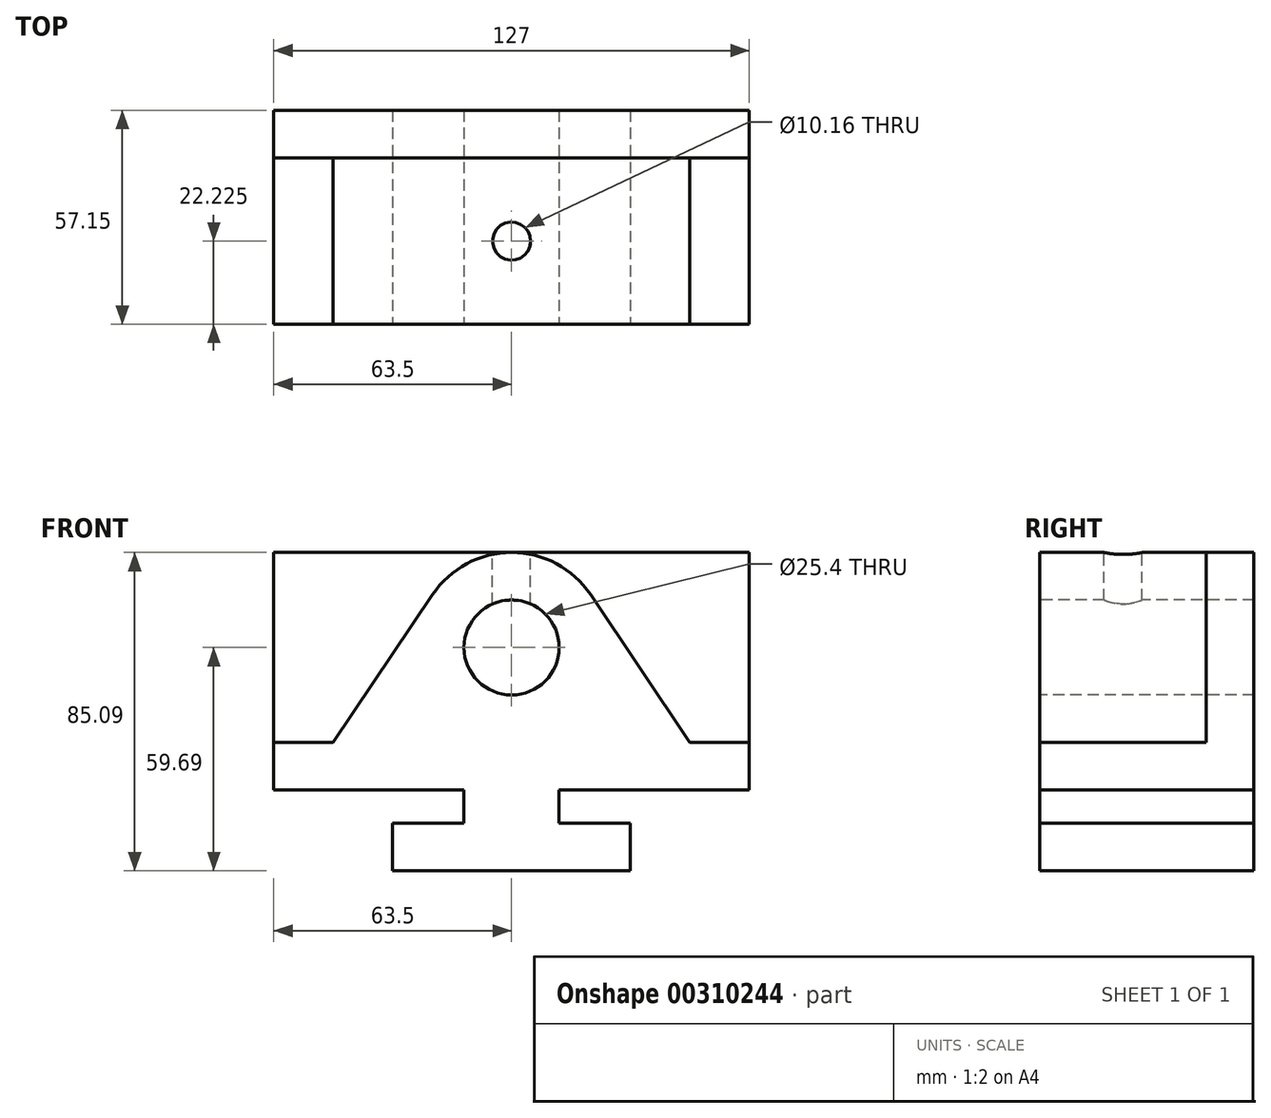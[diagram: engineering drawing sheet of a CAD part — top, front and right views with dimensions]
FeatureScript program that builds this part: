
annotation { "Feature Type Name" : "Feature", "Feature Type Description" : "" }
export const myFeature = defineFeature(function(context is Context, id is Id, definition is map)
    precondition{}
    {
        {
            var Q0;
            Q0=qCreatedBy(makeId("Front.planeOp"),FACE);
            var sketch = newSketch(context, id + "F0", { "sketchPlane" : qUnion([Q0])});
            skLineSegment(sketch, "E0", {"start": v(31.75, 0) * mm, "end": v(-31.75, 0) * mm});
            skLineSegment(sketch, "E1", {"start": v(-31.75, 0) * mm, "end": v(-31.75, 12.7) * mm});
            skLineSegment(sketch, "E2", {"start": v(-31.75, 12.7) * mm, "end": v(-12.7, 12.7) * mm});
            skLineSegment(sketch, "E3", {"start": v(-12.7, 12.7) * mm, "end": v(-12.7, 21.59) * mm});
            skLineSegment(sketch, "E4", {"start": v(-12.7, 21.59) * mm, "end": v(-63.5, 21.59) * mm});
            skLineSegment(sketch, "E5", {"start": v(-63.5, 21.59) * mm, "end": v(-63.5, 85.1) * mm});
            skLineSegment(sketch, "E6", {"start": v(-63.5, 85.1) * mm, "end": v(63.5, 85.1) * mm});
            skLineSegment(sketch, "E7", {"start": v(63.5, 85.1) * mm, "end": v(63.5, 21.6) * mm});
            skLineSegment(sketch, "E8", {"start": v(63.5, 21.6) * mm, "end": v(12.7, 21.59) * mm});
            skLineSegment(sketch, "E9", {"start": v(12.7, 21.59) * mm, "end": v(12.7, 12.7) * mm});
            skLineSegment(sketch, "E10", {"start": v(12.7, 12.7) * mm, "end": v(31.75, 12.7) * mm});
            skLineSegment(sketch, "E11", {"start": v(31.75, 12.7) * mm, "end": v(31.75, 0) * mm});
            skSolve(sketch);
        }
        {
            var Q0;
            Q0 = qSketchRegion(id + "F0", true);
            extrude(context, id + "F1", {"entities" : qUnion([Q0]), "oppositeDirection" : true, "depth" : 57.15 * mm});
        }
        {
            var Q0;
            Q0=makeQuery(id+"F1.opExtrude","CAP_FACE",FACE,{"disambiguationData":[OSD([sQuery(id+"F0.wireOp",EDGE,"E0"),sQuery(id+"F0.wireOp",EDGE,"E1"),sQuery(id+"F0.wireOp",EDGE,"E2"),sQuery(id+"F0.wireOp",EDGE,"E3"),sQuery(id+"F0.wireOp",EDGE,"E4"),sQuery(id+"F0.wireOp",EDGE,"E5"),sQuery(id+"F0.wireOp",EDGE,"E6"),sQuery(id+"F0.wireOp",EDGE,"E7"),sQuery(id+"F0.wireOp",EDGE,"E8"),sQuery(id+"F0.wireOp",EDGE,"E9"),sQuery(id+"F0.wireOp",EDGE,"E10"),sQuery(id+"F0.wireOp",EDGE,"E11")])],"isStart":true});
            var sketch = newSketch(context, id + "F2", { "sketchPlane" : qUnion([Q0])});
            skLineSegment(sketch, "E12", {"start": v(-63.5, 21.59) * mm, "end": v(-63.5, 34.3) * mm});
            skLineSegment(sketch, "E13", {"start": v(-63.5, 34.3) * mm, "end": v(-47.63, 34.3) * mm});
            skLineSegment(sketch, "E14", {"start": v(-47.63, 34.3) * mm, "end": v(-21.1, 73.84) * mm});
            skLineSegment(sketch, "E15", {"start": v(63.5, 21.6) * mm, "end": v(63.5, 34.3) * mm});
            skPoint(sketch, "E15.endSnap0", {"position": v(-55.56, 34.3) * mm});
            skLineSegment(sketch, "E16", {"start": v(63.5, 34.3) * mm, "end": v(47.62, 34.3) * mm});
            skLineSegment(sketch, "E17", {"start": v(47.63, 34.3) * mm, "end": v(21.1, 73.84) * mm});
            skArc(sketch, "E18", {"start": v(21.1, 73.84) * mm, "mid": v(0, 85.1) * mm, "end": v(-21.1, 73.84) * mm});
            skCircle(sketch, "E19", {"center": v(0, 59.7) * mm, "radius": 12.7 * mm});
            skLineSegment(sketch, "E20", {"start": v(-63.5, 34.3) * mm, "end": v(-63.5, 85.1) * mm});
            skLineSegment(sketch, "E21", {"start": v(-63.5, 85.1) * mm, "end": v(0, 85.1) * mm});
            skLineSegment(sketch, "E22", {"start": v(0, 85.1) * mm, "end": v(63.5, 85.1) * mm});
            skLineSegment(sketch, "E23", {"start": v(63.5, 85.1) * mm, "end": v(63.5, 34.3) * mm});
            skSolve(sketch);
        }
        {
            var Q0;
            Q0=makeQuery(id+"F2.imprint","IMPRINT",FACE,{"disambiguationData":[TD([[makeQuery(id+"F2.imprint","IMPRINT",EDGE,{"derivedFrom":sQuery(id+"F2.wireOp",EDGE,"E13")}),1.0]])]});
            var Q1;
            Q1=makeQuery(id+"F2.imprint","IMPRINT",FACE,{"disambiguationData":[TD([[makeQuery(id+"F2.imprint","IMPRINT",EDGE,{"derivedFrom":sQuery(id+"F2.wireOp",EDGE,"E16")}),-1.0]])]});
            extrude(context, id + "F3", {"entities" : qUnion([Q0, Q1]), "operationType" : NewBodyOperationType.REMOVE, "oppositeDirection" : true, "depth" : 44.45 * mm});
        }
        {
            var Q0;
            Q0=makeQuery(id+"F2.imprint","IMPRINT",FACE,{"disambiguationData":[TD([[makeQuery(id+"F2.imprint","IMPRINT",EDGE,{"derivedFrom":sQuery(id+"F2.wireOp",EDGE,"E19")}),1.0]])]});
            extrude(context, id + "F4", {"entities" : qUnion([Q0]), "operationType" : NewBodyOperationType.REMOVE, "endBound" : BoundingType.THROUGH_ALL, "oppositeDirection" : true, "depth" : 25.4 * mm});
        }
        {
            var Q0;
            Q0=makeQuery(id+"F1.opExtrude","SWEPT_FACE",FACE,{"disambiguationData":[OSD([sQuery(id+"F0.wireOp",EDGE,"E6")])]});
            var sketch = newSketch(context, id + "F5", { "sketchPlane" : qUnion([Q0])});
            skCircle(sketch, "E24", {"center": v(0, 22.23) * mm, "radius": 5.08 * mm});
            skSolve(sketch);
        }
        {
            var Q0;
            Q0=makeQuery(id+"F5.imprint","IMPRINT",FACE,{"disambiguationData":[TD([[makeQuery(id+"F5.imprint","IMPRINT",EDGE,{"derivedFrom":sQuery(id+"F5.wireOp",EDGE,"E24")}),1.0]])]});
            extrude(context, id + "F6", {"entities" : qUnion([Q0]), "operationType" : NewBodyOperationType.REMOVE, "oppositeDirection" : true, "depth" : 25.4 * mm});
        }
    });
